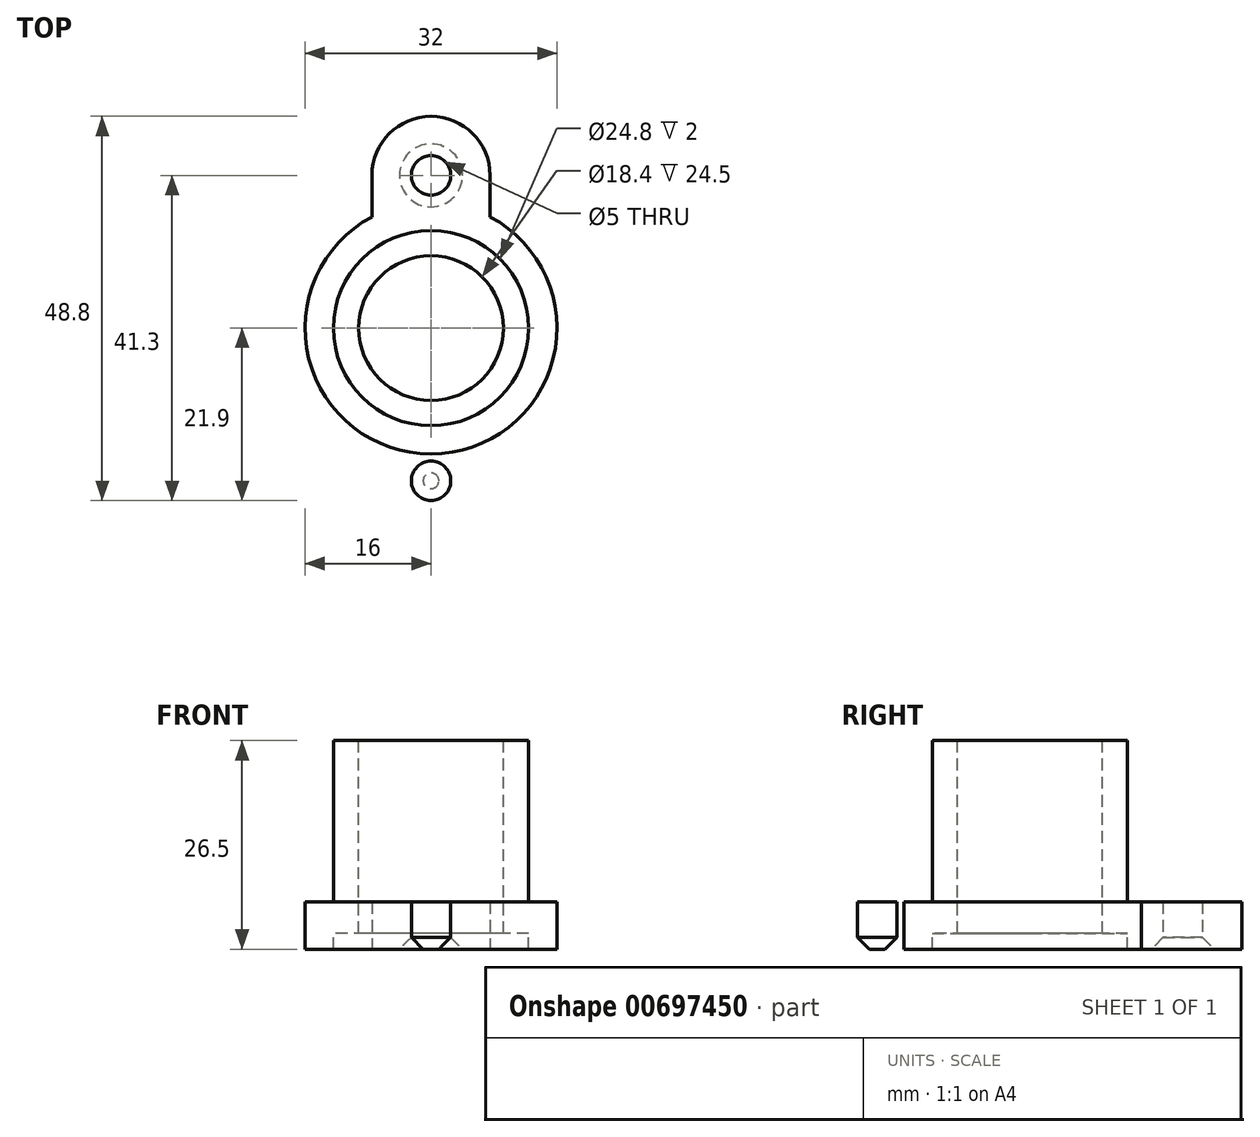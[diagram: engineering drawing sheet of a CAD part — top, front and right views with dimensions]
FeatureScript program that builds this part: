
annotation { "Feature Type Name" : "Feature", "Feature Type Description" : "" }
export const myFeature = defineFeature(function(context is Context, id is Id, definition is map)
    precondition{}
    {
        {
            var Q0;
            Q0=qCreatedBy(makeId("Front.planeOp"),FACE);
            var sketch = newSketch(context, id + "F0", { "sketchPlane" : qUnion([Q0])});
            skLineSegment(sketch, "E0", {"start": v(0, -4.84) * mm, "end": v(16, -4.84) * mm, "construction": true});
            skLineSegment(sketch, "E1", {"start": v(0, -2.24) * mm, "end": v(12.4, -2.24) * mm, "construction": true});
            skLineSegment(sketch, "E2", {"start": v(-2.24, 0) * mm, "end": v(-2.24, 2) * mm, "construction": true});
            skLineSegment(sketch, "E3", {"start": v(-2.95, 0) * mm, "end": v(-2.95, 6) * mm, "construction": true});
            skLineSegment(sketch, "E4", {"start": v(-5.2, 0) * mm, "end": v(-5.2, 26.5) * mm, "construction": true});
            skLineSegment(sketch, "E5", {"start": v(16, -1.12) * mm, "end": v(9.2, -1.12) * mm, "construction": true});
            skLineSegment(sketch, "E6", {"start": v(12.4, 0) * mm, "end": v(12.4, 2) * mm});
            skLineSegment(sketch, "E7", {"start": v(12.4, 2) * mm, "end": v(9.2, 2) * mm});
            skLineSegment(sketch, "E8", {"start": v(9.2, 2) * mm, "end": v(9.2, 26.5) * mm});
            skLineSegment(sketch, "E9", {"start": v(9.2, 26.5) * mm, "end": v(12.4, 26.5) * mm});
            skLineSegment(sketch, "E10", {"start": v(12.4, 26.5) * mm, "end": v(12.4, 6) * mm});
            skLineSegment(sketch, "E11", {"start": v(12.4, 6) * mm, "end": v(16, 6) * mm});
            skLineSegment(sketch, "E12", {"start": v(16, 6) * mm, "end": v(16, 0) * mm});
            skLineSegment(sketch, "E13", {"start": v(16, 0) * mm, "end": v(12.4, 0) * mm});
            skLineSegment(sketch, "E14", {"start": v(0, 37.66) * mm, "end": v(0, -36.6) * mm, "construction": true});
            skSolve(sketch);
        }
        {
            var Q0;
            Q0=makeQuery(id+"F0.imprint","IMPRINT",FACE,{"disambiguationData":[TD([[makeQuery(id+"F0.imprint","IMPRINT",EDGE,{"derivedFrom":sQuery(id+"F0.wireOp",EDGE,"E6")}),-1.0]])]});
            var Q1;
            Q1=sQuery(id+"F0.wireOp",EDGE,"E14");
            revolve(context, id + "F1", {"surfaceOperationType" : NewSurfaceOperationType.NEW, "entities" : qUnion([Q0]), "axis" : qUnion([Q1]), "revolveType" : RevolveType.FULL});
        }
        {
            var Q0;
            Q0=qCreatedBy(makeId("Top.planeOp"),FACE);
            var sketch = newSketch(context, id + "F2", { "sketchPlane" : qUnion([Q0])});
            skLineSegment(sketch, "E15", {"start": v(21.28, 0) * mm, "end": v(21.28, -19.4) * mm, "construction": true});
            skLineSegment(sketch, "E16", {"start": v(21.28, 0) * mm, "end": v(21.28, 19.4) * mm, "construction": true});
            skCircle(sketch, "E17", {"center": v(0, 19.4) * mm, "radius": 2.5 * mm});
            skLineSegment(sketch, "E18", {"start": v(0, 31.96) * mm, "end": v(-7.5, 31.96) * mm, "construction": true});
            skLineSegment(sketch, "E19", {"start": v(-7.5, 31.96) * mm, "end": v(7.5, 31.96) * mm, "construction": true});
            skArc(sketch, "E20", {"start": v(7.5, 19.4) * mm, "mid": v(0, 26.9) * mm, "end": v(-7.5, 19.4) * mm});
            skLineSegment(sketch, "E21", {"start": v(7.5, 19.4) * mm, "end": v(7.5, 14.12) * mm});
            skLineSegment(sketch, "E22.MirrorCS", {"start": v(-7.5, 19.4) * mm, "end": v(-7.5, 14.12) * mm});
            skCircle(sketch, "E23.0", {"center": v(0, 0) * mm, "radius": 16 * mm});
            skCircle(sketch, "E24.MirrorC", {"center": v(0, -19.4) * mm, "radius": 2.5 * mm});
            skArc(sketch, "E25.MirrorCS", {"start": v(7.5, -19.4) * mm, "mid": v(0, -26.9) * mm, "end": v(-7.5, -19.4) * mm});
            skLineSegment(sketch, "E26.MirrorCS", {"start": v(-7.5, -19.4) * mm, "end": v(-7.5, -14.12) * mm});
            skLineSegment(sketch, "E27.MirrorCS", {"start": v(7.5, -19.4) * mm, "end": v(7.5, -14.12) * mm});
            skSolve(sketch);
        }
        {
            var Q0;
            Q0=makeQuery(id+"F2.imprint","IMPRINT",FACE,{"disambiguationData":[TD([[makeQuery(id+"F2.imprint","IMPRINT",EDGE,{"derivedFrom":sQuery(id+"F2.wireOp",EDGE,"E17")}),-1.0]])]});
            var Q1;
            Q1=makeQuery(id+"F2.imprint","IMPRINT",FACE,{"disambiguationData":[TD([[makeQuery(id+"F2.imprint","IMPRINT",EDGE,{"derivedFrom":sQuery(id+"F2.wireOp",EDGE,"E24.MirrorC")}),1.0]])]});
            extrude(context, id + "F3", {"entities" : qUnion([Q0, Q1]), "operationType" : NewBodyOperationType.ADD, "depth" : 6 * mm, "offsetDistance" : 25 * mm});
        }
        {
            var Q0;
            Q0=makeQuery(id+"F3.opExtrude","CAP_EDGE",EDGE,{"disambiguationData":[OSD([sQuery(id+"F2.wireOp",EDGE,"E17")])],"isStart":true});
            var Q1;
            Q1=makeQuery(id+"F3.opExtrude","CAP_EDGE",EDGE,{"disambiguationData":[OSD([sQuery(id+"F2.wireOp",EDGE,"E24.MirrorC")])],"isStart":true});
            chamfer(context, id + "F4", {"entities" : qUnion([Q0, Q1]), "width" : 1.5 * mm, "tangentPropagation" : true});
        }
    });
